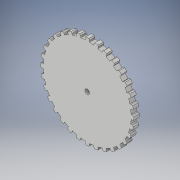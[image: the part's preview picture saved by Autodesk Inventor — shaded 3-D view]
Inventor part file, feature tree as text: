
AUTODESK INVENTOR PART (.ipt)
format: ipt  version: 2017 (Build 210142000, 142)  size: 338,432 bytes
history: native  units: in
note: dims shown in document units (in); Inventor stores cm internally (conversion verified against a paired STEP export)
features: extrude x2, sketch x2, pattern_circular x1
ambient origin geometry x8: Origin, YZ Plane, XZ Plane, XY Plane, X Axis, Y Axis, Z Axis, Center Point
bodies: Body1 (feature_tree)
feature tree (5):
  extrude  "Extrusion2"  Depth=0.075in
  pattern_circular  "Circular Pattern2"  Count=128 Angle=360.0deg
  extrude  "Extrusion3"  Depth=0.15in TaperAngle=0.0deg
  sketch  "Sketch1"  dims[d0=2.4in d10=0.075in]
  sketch  "Sketch2"  dims[d11=0.04in d12=50.3937in d14=360.0deg d16=0.15in d17=0.0in d18=12.5984in d19=360.0deg d21=0.126in d22=1.0in d23=0.0in]
